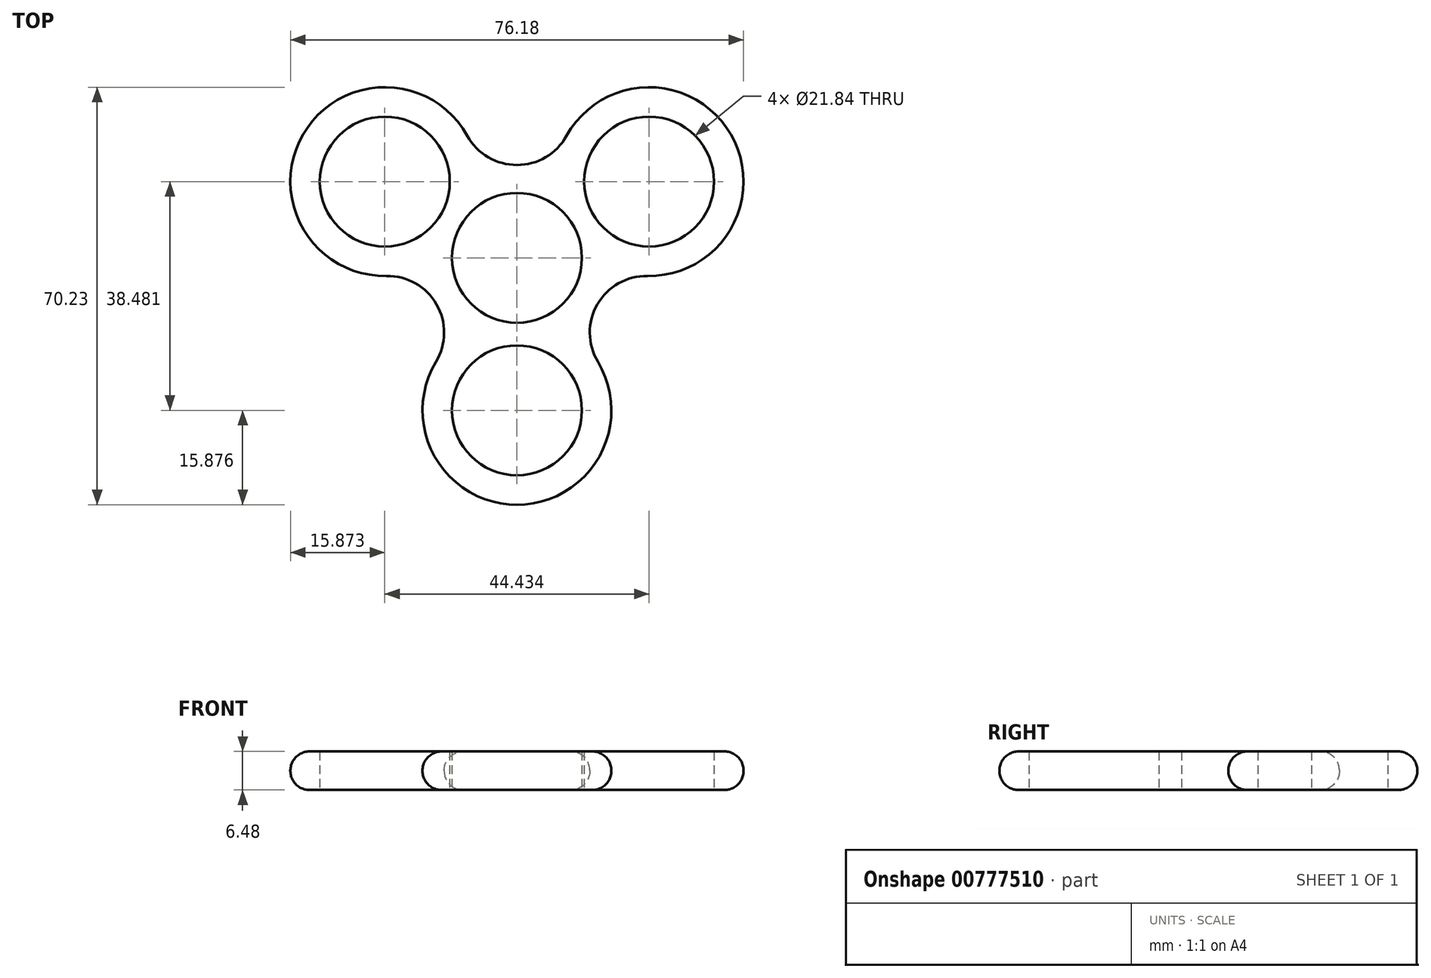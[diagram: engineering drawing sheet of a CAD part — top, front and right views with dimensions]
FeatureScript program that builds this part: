
annotation { "Feature Type Name" : "Feature", "Feature Type Description" : "" }
export const myFeature = defineFeature(function(context is Context, id is Id, definition is map)
    precondition{}
    {
        {
            var Q0;
            Q0=qCreatedBy(makeId("Top.planeOp"),FACE);
            var sketch = newSketch(context, id + "F0", { "sketchPlane" : qUnion([Q0])});
            skCircle(sketch, "E0", {"center": v(0, 0) * mm, "radius": 10.92 * mm});
            skCircle(sketch, "E1", {"center": v(-22.22, 12.83) * mm, "radius": 10.92 * mm});
            skCircle(sketch, "E2", {"center": v(22.22, 12.83) * mm, "radius": 10.92 * mm});
            skCircle(sketch, "E3", {"center": v(0, -25.65) * mm, "radius": 10.92 * mm});
            skLineSegment(sketch, "E4", {"start": v(0, 0) * mm, "end": v(-22.22, 12.83) * mm, "construction": true});
            skLineSegment(sketch, "E5", {"start": v(0, 0) * mm, "end": v(22.22, 12.83) * mm, "construction": true});
            skArc(sketch, "E6", {"start": v(-8.33, 20.52) * mm, "mid": v(-35.97, 20.76) * mm, "end": v(-21.94, -3.05) * mm});
            skArc(sketch, "E7", {"start": v(21.94, -3.05) * mm, "mid": v(35.97, 20.76) * mm, "end": v(8.33, 20.52) * mm});
            skArc(sketch, "E8", {"start": v(-13.6, -17.48) * mm, "mid": v(0, -41.53) * mm, "end": v(13.6, -17.48) * mm});
            skPoint(sketch, "E9.visualSharp", {"position": v(17.53, -2.34) * mm});
            skPoint(sketch, "E10.visualSharp", {"position": v(10.8, -14.01) * mm});
            skArc(sketch, "E11", {"start": v(-13.6, -17.48) * mm, "mid": v(-13.52, -7.8) * mm, "end": v(-21.94, -3.05) * mm});
            skArc(sketch, "E12", {"start": v(21.94, -3.05) * mm, "mid": v(13.52, -7.8) * mm, "end": v(13.6, -17.48) * mm});
            skArc(sketch, "E13", {"start": v(-8.33, 20.52) * mm, "mid": v(0, 15.61) * mm, "end": v(8.33, 20.52) * mm});
            skSolve(sketch);
        }
        {
            var Q0;
            Q0=makeQuery(id+"F0.imprint","IMPRINT",FACE,{"disambiguationData":[TD([[makeQuery(id+"F0.imprint","IMPRINT",EDGE,{"derivedFrom":sQuery(id+"F0.wireOp",EDGE,"E0")}),-1.0]])]});
            extrude(context, id + "F1", {"entities" : qUnion([Q0]), "depth" : 6.48 * mm, "offsetDistance" : 25.4 * mm});
        }
        {
            var Q0;
            Q0=makeQuery(id+"F1.opExtrude","CAP_EDGE",EDGE,{"disambiguationData":[OSD([sQuery(id+"F0.wireOp",EDGE,"E6")])],"isStart":false});
            fillet(context, id + "F2", {"entities" : qUnion([Q0]), "radius" : 3.17 * mm, "tangentPropagation" : true, "allowEdgeOverflow" : false});
        }
        {
            var Q0;
            Q0=makeQuery(id+"F1.opExtrude","CAP_EDGE",EDGE,{"disambiguationData":[OSD([sQuery(id+"F0.wireOp",EDGE,"E8")])],"isStart":true});
            fillet(context, id + "F3", {"entities" : qUnion([Q0]), "radius" : 3.17 * mm, "tangentPropagation" : true, "allowEdgeOverflow" : false});
        }
    });
